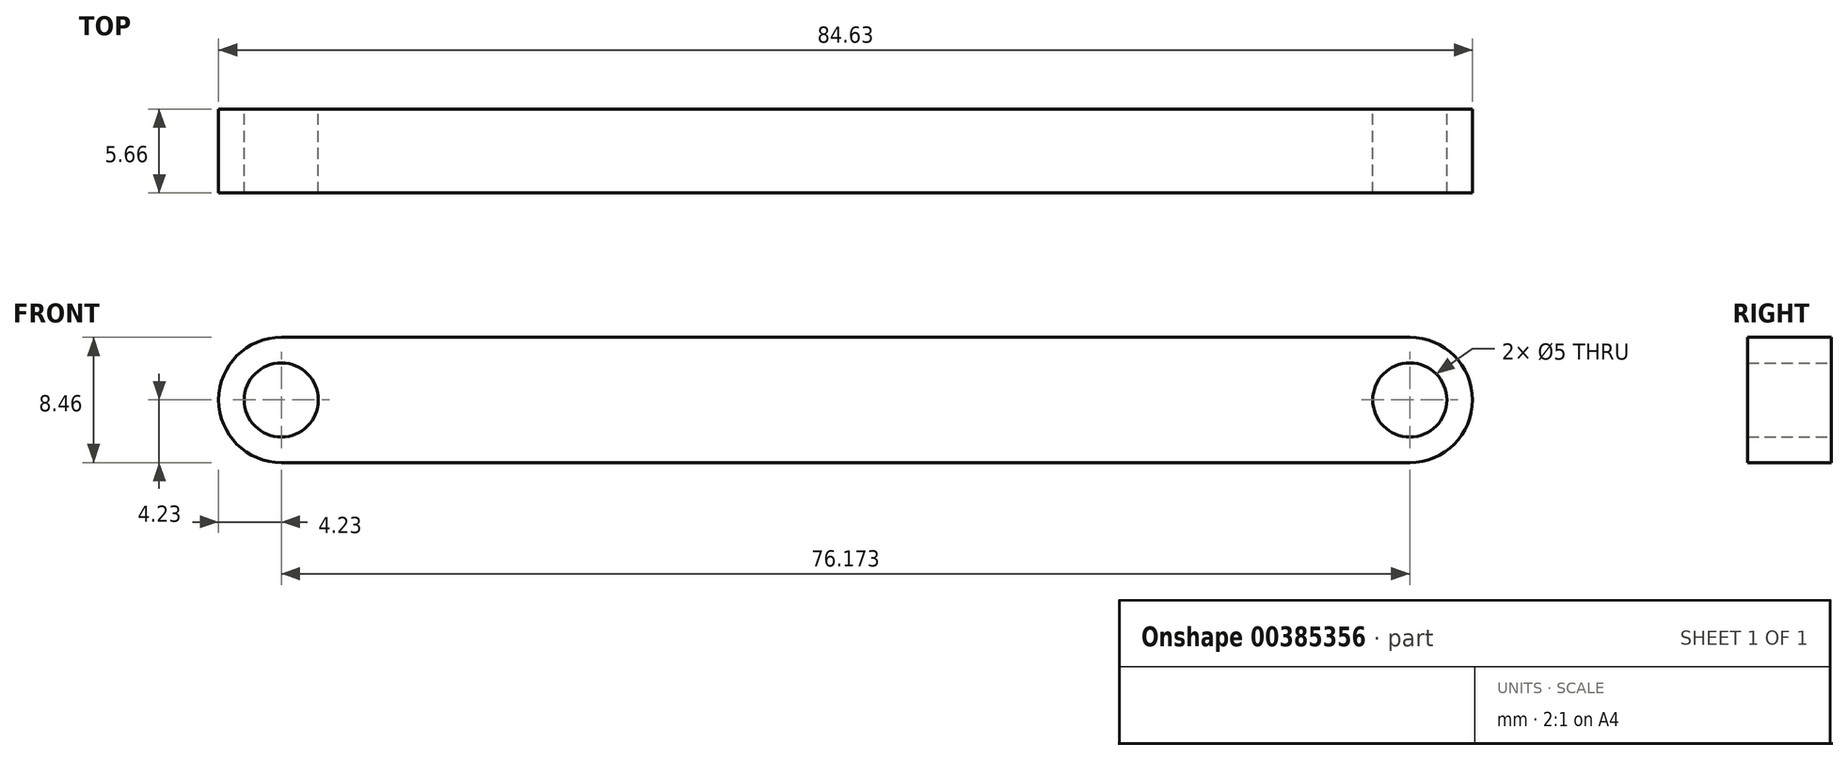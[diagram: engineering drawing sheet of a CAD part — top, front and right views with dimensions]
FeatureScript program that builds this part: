
annotation { "Feature Type Name" : "Feature", "Feature Type Description" : "" }
export const myFeature = defineFeature(function(context is Context, id is Id, definition is map)
    precondition{}
    {
        {
            var Q0;
            Q0=qCreatedBy(makeId("Front.planeOp"),FACE);
            var sketch = newSketch(context, id + "F0", { "sketchPlane" : qUnion([Q0])});
            skCircle(sketch, "E0", {"center": v(0, 0) * mm, "radius": 2.5 * mm});
            skArc(sketch, "E1", {"start": v(0, 4.23) * mm, "mid": v(-4.23, 0) * mm, "end": v(0, -4.23) * mm});
            skCircle(sketch, "E2", {"center": v(76.17, 0) * mm, "radius": 2.5 * mm});
            skArc(sketch, "E3", {"start": v(76.17, -4.23) * mm, "mid": v(80.4, 0) * mm, "end": v(76.17, 4.23) * mm});
            skLineSegment(sketch, "E4", {"start": v(0, 4.23) * mm, "end": v(76.17, 4.23) * mm});
            skLineSegment(sketch, "E5", {"start": v(0, -4.23) * mm, "end": v(76.17, -4.23) * mm});
            skSolve(sketch);
        }
        {
            var Q0;
            Q0 = qSketchRegion(id + "F0", true);
            extrude(context, id + "F1", {"entities" : qUnion([Q0]), "depth" : 5.66 * mm});
        }
    });
